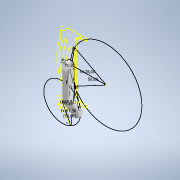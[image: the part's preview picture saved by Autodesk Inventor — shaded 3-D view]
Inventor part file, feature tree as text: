
AUTODESK INVENTOR PART (.ipt)
format: ipt  version: 2022 (Build 260153000, 153)  size: 274,432 bytes
history: native  units: mm
features: reference x11, fillet x9, other x8, sketch x4, extrude x3, projected_geometry x2, chamfer x1
ambient origin geometry x8: Origin, YZ Plane, XZ Plane, XY Plane, X Axis, Y Axis, Z Axis, Center Point
bodies: Body1 (feature_tree)
feature tree (38):
  other  "Твердое тело1"
  sketch  "Эскиз1"
  extrude  "Выдавливание1"  Depth=2.2mm
  fillet  "Сопряжение1"  Radius=6.0mm
  fillet  "Сопряжение2"  Radius=9.773844mm
  extrude  "Выдавливание2"  Depth=4.886922mm
  fillet  "Сопряжение3"  Radius=28.0mm
  fillet  "Сопряжение4"  Radius=28.0mm
  extrude  "Выдавливание3"  Depth=28.0mm
  fillet  "Сопряжение5"  Radius=28.0mm
  fillet  "Сопряжение6"  Radius=23.511846mm
  fillet  "Сопряжение7"  Radius=11.755923mm
  chamfer  "Фаска1"  Distance=5.0mm
  fillet  "Сопряжение8"  Radius=6.0mm
  fillet  "Сопряжение9"  Radius=0.5mm
  reference  "Ссылка1"
  reference  "Ссылка3"
  reference  "Ссылка4"
  sketch  "Эскиз2"
  reference  "Ссылка5"
  reference  "Ссылка6"
  reference  "Ссылка7"
  reference  "Ссылка8"
  reference  "Ссылка9"
  sketch  "Эскиз4"
  projected_geometry  "Спроецированная петля2"
  reference  "Ссылка10"
  reference  "Ссылка11"
  reference  "Ссылка12"
  sketch  "Эскиз5"
  projected_geometry  "Спроецированная петля3"
  other  "<userpath>\Documents\Git\MZCAT_2024\MZCAT_4.iam"
  other  "MZCAT_4.iam"
  other  "lidar_krestovina:1"
  other  "lidar_shatun_main:1"
  other  "lidar_krestovina_base:1"
  other  "OCS-D008 B:3"
  other  "lever_lidar:1"
